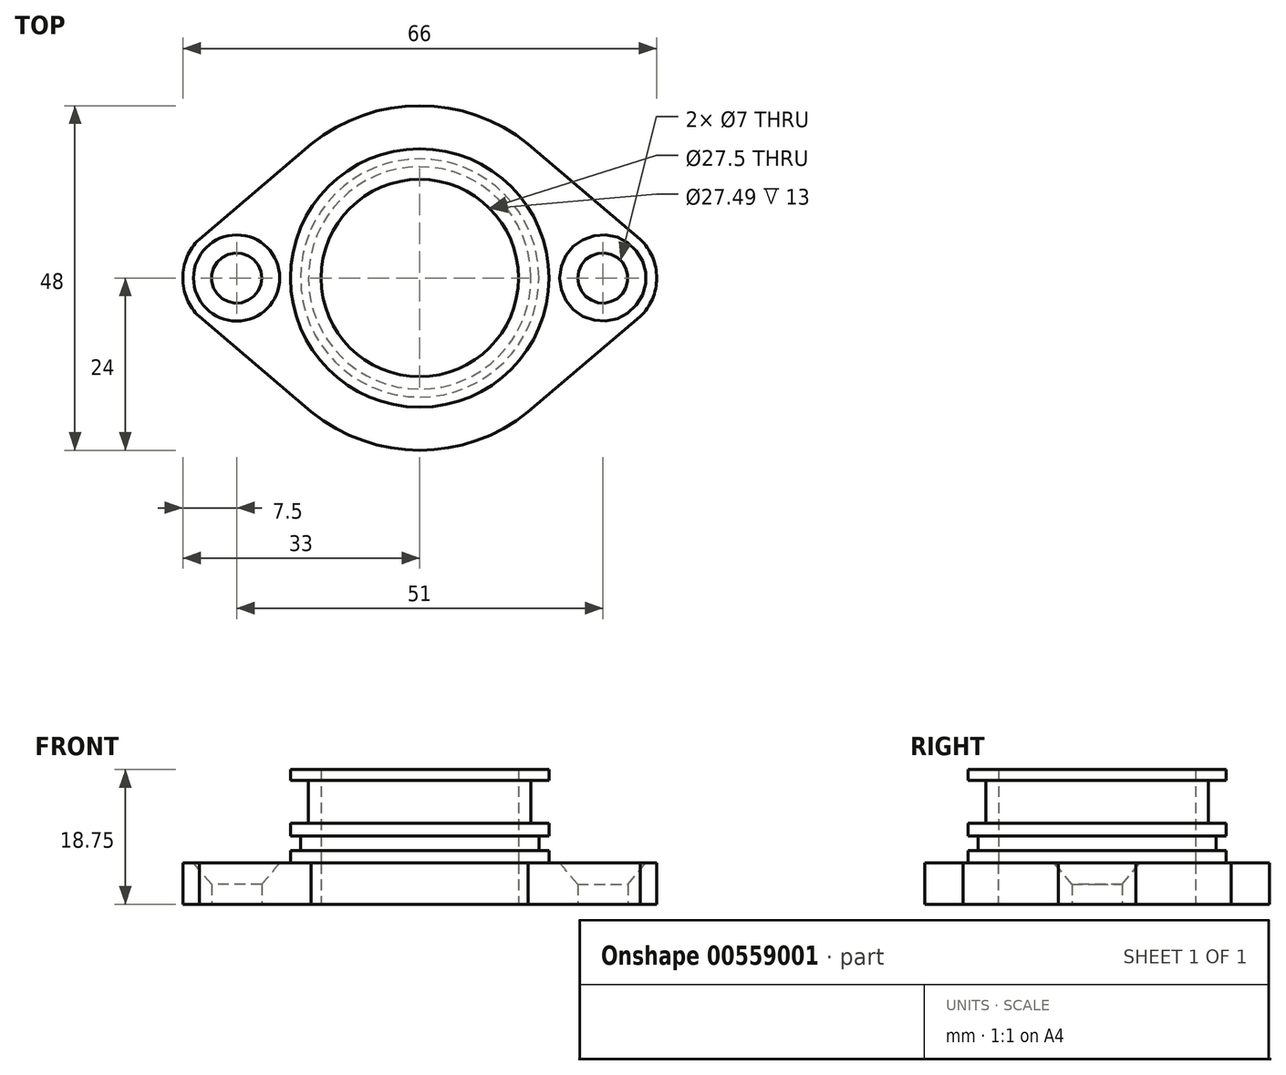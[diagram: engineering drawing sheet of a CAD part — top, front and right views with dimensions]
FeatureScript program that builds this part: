
annotation { "Feature Type Name" : "Feature", "Feature Type Description" : "" }
export const myFeature = defineFeature(function(context is Context, id is Id, definition is map)
    precondition{}
    {
        {
            var Q0;
            Q0=qCreatedBy(makeId("Top.planeOp"),FACE);
            var sketch = newSketch(context, id + "F0", { "sketchPlane" : qUnion([Q0])});
            skCircle(sketch, "E0", {"center": v(0, 0) * mm, "radius": 18 * mm});
            skCircle(sketch, "E1", {"center": v(0, 0) * mm, "radius": 13.75 * mm});
            skCircle(sketch, "E2", {"center": v(0, 0) * mm, "radius": 24 * mm});
            skCircle(sketch, "E3", {"center": v(-25.5, 0) * mm, "radius": 3.5 * mm});
            skCircle(sketch, "E4.MirrorC", {"center": v(25.5, 0) * mm, "radius": 3.5 * mm});
            skCircle(sketch, "E5", {"center": v(-25.5, 0) * mm, "radius": 7.5 * mm});
            skCircle(sketch, "E6", {"center": v(25.5, 0) * mm, "radius": 7.5 * mm});
            skLineSegment(sketch, "E7", {"start": v(-30.72, -5.39) * mm, "end": v(-15.12, -18.64) * mm});
            skLineSegment(sketch, "E8.MirrorCS", {"start": v(-30.72, 5.39) * mm, "end": v(-15.12, 18.64) * mm});
            skLineSegment(sketch, "E9.MirrorCS", {"start": v(30.72, 5.39) * mm, "end": v(15.12, 18.64) * mm});
            skLineSegment(sketch, "E10.MirrorCS", {"start": v(30.72, -5.39) * mm, "end": v(15.12, -18.64) * mm});
            skSolve(sketch);
        }
        {
            var Q0;
            Q0=makeQuery(id+"F0.imprint","IMPRINT",FACE,{"disambiguationData":[TD([[makeQuery(id+"F0.imprint","IMPRINT",EDGE,{"derivedFrom":sQuery(id+"F0.wireOp",EDGE,"E1")}),-1.0]])]});
            var Q1;
            {var subQ6=sQuery(id+"F0.wireOp",EDGE,"E5");var subQ8=sQuery(id+"F0.wireOp",EDGE,"E0");var subQ9=makeQuery(id+"F0.imprint","INTERSECT",VERTEX,{"derivedFrom":[subQ8,subQ6]});Q1=makeQuery(id+"F0.imprint","IMPRINT",FACE,{"disambiguationData":[TD([[makeQuery(id+"F0.imprint","IMPRINT",EDGE,{"disambiguationData":[TD([[subQ9,-1.0]])],"derivedFrom":subQ8}),-1.0]])]});}
            var Q2;
            {var subQ3=sQuery(id+"F0.wireOp",EDGE,"E5");var subQ11=sQuery(id+"F0.wireOp",EDGE,"E0");var subQ12=makeQuery(id+"F0.imprint","INTERSECT",VERTEX,{"derivedFrom":[subQ11,subQ3]});Q2=makeQuery(id+"F0.imprint","IMPRINT",FACE,{"disambiguationData":[TD([[makeQuery(id+"F0.imprint","IMPRINT",EDGE,{"disambiguationData":[TD([[subQ12,1.0]])],"derivedFrom":subQ11}),-1.0]])]});}
            var Q3;
            {var subQ0=sQuery(id+"F0.wireOp",EDGE,"E5");var subQ2=sQuery(id+"F0.wireOp",EDGE,"E2");var subQ3=makeQuery(id+"F0.imprint","INTERSECT",VERTEX,{"disambiguationData":[OD(0.0)],"derivedFrom":[subQ2,subQ0]});Q3=makeQuery(id+"F0.imprint","IMPRINT",FACE,{"disambiguationData":[TD([[makeQuery(id+"F0.imprint","IMPRINT",EDGE,{"disambiguationData":[TD([[subQ3,-1.0]])],"derivedFrom":subQ2}),1.0]])]});}
            var Q4;
            {var subQ1=sQuery(id+"F0.wireOp",EDGE,"E2");var subQ3=sQuery(id+"F0.wireOp",EDGE,"E5");var subQ7=makeQuery(id+"F0.imprint","INTERSECT",VERTEX,{"disambiguationData":[OD(0.0)],"derivedFrom":[subQ1,subQ3]});Q4=makeQuery(id+"F0.imprint","IMPRINT",FACE,{"disambiguationData":[TD([[makeQuery(id+"F0.imprint","IMPRINT",EDGE,{"disambiguationData":[TD([[subQ7,-1.0]])],"derivedFrom":subQ1}),-1.0]])]});}
            var Q5;
            {var subQ0=sQuery(id+"F0.wireOp",EDGE,"E8.MirrorCS");var subQ1=sQuery(id+"F0.wireOp",EDGE,"E2");var subQ2=makeQuery(id+"F0.imprint","INTERSECT",VERTEX,{"disambiguationData":[OD(1.0)],"derivedFrom":[subQ1,subQ0]});Q5=makeQuery(id+"F0.imprint","IMPRINT",FACE,{"disambiguationData":[TD([[makeQuery(id+"F0.imprint","IMPRINT",EDGE,{"disambiguationData":[TD([[subQ2,-1.0]])],"derivedFrom":subQ1}),-1.0]])]});}
            var Q6;
            {var subQ0=sQuery(id+"F0.wireOp",EDGE,"E7");var subQ1=sQuery(id+"F0.wireOp",EDGE,"E2");var subQ2=makeQuery(id+"F0.imprint","INTERSECT",VERTEX,{"disambiguationData":[OD(1.0)],"derivedFrom":[subQ1,subQ0]});Q6=makeQuery(id+"F0.imprint","IMPRINT",FACE,{"disambiguationData":[TD([[makeQuery(id+"F0.imprint","IMPRINT",EDGE,{"disambiguationData":[TD([[subQ2,1.0]])],"derivedFrom":subQ1}),-1.0]])]});}
            var Q7;
            {var subQ0=sQuery(id+"F0.wireOp",EDGE,"E10.MirrorCS");var subQ1=sQuery(id+"F0.wireOp",EDGE,"E2");var subQ2=makeQuery(id+"F0.imprint","INTERSECT",VERTEX,{"disambiguationData":[OD(1.0)],"derivedFrom":[subQ1,subQ0]});Q7=makeQuery(id+"F0.imprint","IMPRINT",FACE,{"disambiguationData":[TD([[makeQuery(id+"F0.imprint","IMPRINT",EDGE,{"disambiguationData":[TD([[subQ2,-1.0]])],"derivedFrom":subQ1}),-1.0]])]});}
            var Q8;
            {var subQ0=sQuery(id+"F0.wireOp",EDGE,"E6");var subQ2=sQuery(id+"F0.wireOp",EDGE,"E2");var subQ3=makeQuery(id+"F0.imprint","INTERSECT",VERTEX,{"disambiguationData":[OD(0.0)],"derivedFrom":[subQ2,subQ0]});Q8=makeQuery(id+"F0.imprint","IMPRINT",FACE,{"disambiguationData":[TD([[makeQuery(id+"F0.imprint","IMPRINT",EDGE,{"disambiguationData":[TD([[subQ3,1.0]])],"derivedFrom":subQ2}),1.0]])]});}
            var Q9;
            {var subQ1=sQuery(id+"F0.wireOp",EDGE,"E6");var subQ3=sQuery(id+"F0.wireOp",EDGE,"E2");var subQ4=makeQuery(id+"F0.imprint","INTERSECT",VERTEX,{"disambiguationData":[OD(0.0)],"derivedFrom":[subQ3,subQ1]});Q9=makeQuery(id+"F0.imprint","IMPRINT",FACE,{"disambiguationData":[TD([[makeQuery(id+"F0.imprint","IMPRINT",EDGE,{"disambiguationData":[TD([[subQ4,1.0]])],"derivedFrom":subQ3}),-1.0]])]});}
            var Q10;
            {var subQ0=sQuery(id+"F0.wireOp",EDGE,"E9.MirrorCS");var subQ1=sQuery(id+"F0.wireOp",EDGE,"E2");var subQ2=makeQuery(id+"F0.imprint","INTERSECT",VERTEX,{"disambiguationData":[OD(1.0)],"derivedFrom":[subQ1,subQ0]});Q10=makeQuery(id+"F0.imprint","IMPRINT",FACE,{"disambiguationData":[TD([[makeQuery(id+"F0.imprint","IMPRINT",EDGE,{"disambiguationData":[TD([[subQ2,1.0]])],"derivedFrom":subQ1}),-1.0]])]});}
            extrude(context, id + "F1", {"entities" : qUnion([Q0, Q1, Q2, Q3, Q4, Q5, Q6, Q7, Q8, Q9, Q10]), "depth" : 5.5 * mm, "offsetDistance" : 25 * mm, "hasSecondDirection" : true, "secondDirectionOppositeDirection" : true, "secondDirectionDepth" : 0.25 * mm});
        }
        {
            var Q0;
            Q0=qCreatedBy(makeId("Front.planeOp"),FACE);
            var sketch = newSketch(context, id + "F2", { "sketchPlane" : qUnion([Q0])});
            skLineSegment(sketch, "E11", {"start": v(-22, 5.5) * mm, "end": v(-19.5, 5.5) * mm});
            skLineSegment(sketch, "E12", {"start": v(-19.5, 5.5) * mm, "end": v(-22, 2.5) * mm});
            skLineSegment(sketch, "E13", {"start": v(-22, 2.5) * mm, "end": v(-22, 5.5) * mm});
            skSolve(sketch);
        }
        {
            var Q0;
            Q0 = qSketchRegion(id + "F2", true);
            var Q1;
            Q1=makeQuery(id+"F1.opExtrude","CAP_EDGE",EDGE,{"disambiguationData":[OSD([sQuery(id+"F0.wireOp",EDGE,"E3")])],"isStart":false});
            revolve(context, id + "F3", {"operationType" : NewBodyOperationType.REMOVE, "entities" : qUnion([Q0]), "axis" : qUnion([Q1]), "revolveType" : RevolveType.FULL, "oppositeDirection" : true});
        }
        {
            var Q0;
            Q0=qCreatedBy(makeId("Front.planeOp"),FACE);
            var sketch = newSketch(context, id + "F4", { "sketchPlane" : qUnion([Q0])});
            skLineSegment(sketch, "E14", {"start": v(29, 5.5) * mm, "end": v(29, 2.5) * mm});
            skLineSegment(sketch, "E15", {"start": v(29, 2.5) * mm, "end": v(31.5, 5.5) * mm});
            skLineSegment(sketch, "E16", {"start": v(31.5, 5.5) * mm, "end": v(29, 5.5) * mm});
            skSolve(sketch);
        }
        {
            var Q0;
            Q0 = qSketchRegion(id + "F4", true);
            var Q1;
            Q1=makeQuery(id+"F1.opExtrude","CAP_EDGE",EDGE,{"disambiguationData":[OSD([sQuery(id+"F0.wireOp",EDGE,"E4.MirrorC")])],"isStart":false});
            revolve(context, id + "F5", {"operationType" : NewBodyOperationType.REMOVE, "entities" : qUnion([Q0]), "axis" : qUnion([Q1]), "revolveType" : RevolveType.FULL});
        }
        {
            var Q0;
            Q0=qCreatedBy(makeId("Front.planeOp"),FACE);
            var sketch = newSketch(context, id + "F6", { "sketchPlane" : qUnion([Q0])});
            skLineSegment(sketch, "E17", {"start": v(13.75, 5.5) * mm, "end": v(13.75, 18.5) * mm});
            skLineSegment(sketch, "E18", {"start": v(13.75, 18.5) * mm, "end": v(18, 18.5) * mm});
            skLineSegment(sketch, "E19", {"start": v(18, 18.5) * mm, "end": v(18, 17) * mm});
            skLineSegment(sketch, "E20", {"start": v(18, 17) * mm, "end": v(15.5, 17) * mm});
            skLineSegment(sketch, "E21", {"start": v(15.5, 17) * mm, "end": v(15.5, 11) * mm});
            skLineSegment(sketch, "E22", {"start": v(15.5, 11) * mm, "end": v(18, 11) * mm});
            skLineSegment(sketch, "E23", {"start": v(18, 11) * mm, "end": v(18, 9.25) * mm});
            skLineSegment(sketch, "E24", {"start": v(18, 9.25) * mm, "end": v(16.6, 9.25) * mm});
            skLineSegment(sketch, "E25", {"start": v(16.6, 9.25) * mm, "end": v(16.6, 7.25) * mm});
            skLineSegment(sketch, "E26", {"start": v(16.6, 7.25) * mm, "end": v(18, 7.25) * mm});
            skLineSegment(sketch, "E27", {"start": v(18, 7.25) * mm, "end": v(18, 5.5) * mm});
            skLineSegment(sketch, "E28", {"start": v(18, 5.5) * mm, "end": v(13.75, 5.5) * mm});
            skSolve(sketch);
        }
        {
            var Q0;
            Q0=makeQuery(id+"F6.imprint","IMPRINT",FACE,{"disambiguationData":[TD([[makeQuery(id+"F6.imprint","IMPRINT",EDGE,{"derivedFrom":sQuery(id+"F6.wireOp",EDGE,"E17")}),-1.0]])]});
            var Q1;
            Q1=makeQuery(id+"F1.opExtrude","CAP_EDGE",EDGE,{"disambiguationData":[OSD([sQuery(id+"F0.wireOp",EDGE,"E1")])],"isStart":false});
            revolve(context, id + "F7", {"operationType" : NewBodyOperationType.ADD, "entities" : qUnion([Q0]), "axis" : qUnion([Q1]), "revolveType" : RevolveType.FULL});
        }
    });
